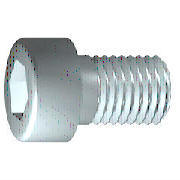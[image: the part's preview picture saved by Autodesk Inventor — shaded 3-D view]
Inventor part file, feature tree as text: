
AUTODESK INVENTOR PART (.ipt)
format: ipt  version: 2024.2 (Build 282272000, 272)  size: 190,976 bytes
history: native  units: mm (DEFAULTED — no unit token found)
features: extrude x1, plane x1, fillet x1, thread x1
ambient origin geometry x7: Origin, YZ Plane, XY Plane, X Axis, Y Axis, Z Axis, Center Point
bodies: Solid1 (feature_tree), Body (feature_tree)
feature tree (4):
  extrude  "Slot"  Depth=10.75mm
  plane  "Work Plane1"
  fillet  "Fillet2"  Radius=0.306825mm
  thread  "Thread2"  [1 undecoded]
note: 1 required parameter value undecoded (feature->parameter linkage not recoverable at this tier; creation-order binding heuristic only, values carry confidence <= 0.55)
